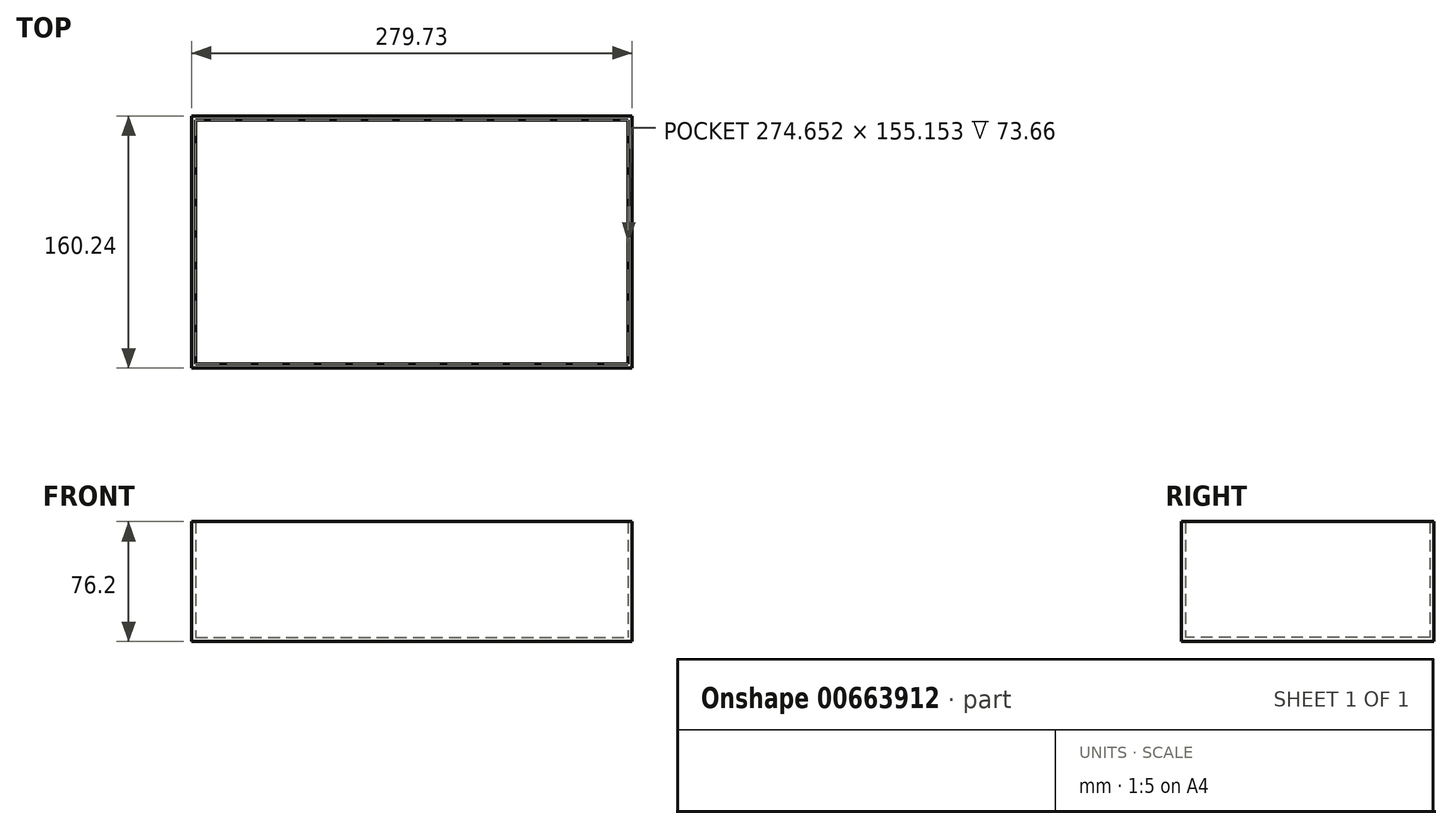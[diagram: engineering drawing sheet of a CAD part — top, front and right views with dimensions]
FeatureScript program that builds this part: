
annotation { "Feature Type Name" : "Feature", "Feature Type Description" : "" }
export const myFeature = defineFeature(function(context is Context, id is Id, definition is map)
    precondition{}
    {
        {
            var Q0;
            Q0=qCreatedBy(makeId("Right.planeOp"),FACE);
            var sketch = newSketch(context, id + "F0", { "sketchPlane" : qUnion([Q0])});
            skLineSegment(sketch, "E0.bottom", {"start": v(-105.78, 33) * mm, "end": v(26.82, 33) * mm});
            skLineSegment(sketch, "E0.top", {"start": v(-105.78, -57.7) * mm, "end": v(26.82, -57.7) * mm});
            skLineSegment(sketch, "E0.left", {"start": v(-105.78, 33) * mm, "end": v(-105.78, -57.7) * mm});
            skLineSegment(sketch, "E0.right", {"start": v(26.82, 33) * mm, "end": v(26.82, -57.7) * mm});
            skSolve(sketch);
        }
        {
            var Q0;
            Q0 = qSketchRegion(id + "F0", true);
            extrude(context, id + "F1", {"entities" : qUnion([Q0]), "depth" : 76.2 * mm, "offsetDistance" : 25.4 * mm});
        }
        {
            var Q0;
            Q0=makeQuery(id+"F1.opExtrude","SWEPT_BODY",BODY,{"disambiguationData":[OSD([sQuery(id+"F0.wireOp",EDGE,"E0.bottom"),sQuery(id+"F0.wireOp",EDGE,"E0.top"),sQuery(id+"F0.wireOp",EDGE,"E0.left"),sQuery(id+"F0.wireOp",EDGE,"E0.right")])]});
            deleteBodies(context, id + "F2", {"entities" : qUnion([Q0])});
        }
        {
            var Q0;
            Q0=qCreatedBy(makeId("Top.planeOp"),FACE);
            var sketch = newSketch(context, id + "F3", { "sketchPlane" : qUnion([Q0])});
            skLineSegment(sketch, "E1.bottom", {"start": v(-160.94, 108.93) * mm, "end": v(118.8, 108.93) * mm});
            skLineSegment(sketch, "E1.top", {"start": v(-160.94, -51.3) * mm, "end": v(118.8, -51.3) * mm});
            skLineSegment(sketch, "E1.left", {"start": v(-160.94, 108.93) * mm, "end": v(-160.94, -51.3) * mm});
            skLineSegment(sketch, "E1.right", {"start": v(118.8, 108.93) * mm, "end": v(118.8, -51.3) * mm});
            skSolve(sketch);
        }
        {
            var Q0;
            Q0=makeQuery(id+"F3.imprint","IMPRINT",FACE,{"disambiguationData":[TD([[makeQuery(id+"F3.imprint","IMPRINT",EDGE,{"derivedFrom":sQuery(id+"F3.wireOp",EDGE,"E1.bottom")}),-1.0]])]});
            extrude(context, id + "F4", {"entities" : qUnion([Q0]), "depth" : 76.2 * mm, "offsetDistance" : 25.4 * mm});
        }
        {
            var Q0;
            Q0=makeQuery(id+"F4.opExtrude","CAP_FACE",FACE,{"disambiguationData":[OSD([sQuery(id+"F3.wireOp",EDGE,"E1.bottom"),sQuery(id+"F3.wireOp",EDGE,"E1.top"),sQuery(id+"F3.wireOp",EDGE,"E1.left"),sQuery(id+"F3.wireOp",EDGE,"E1.right")])],"isStart":false});
            shell(context, id + "F5", {"entities" : qUnion([Q0]), "thickness" : 2.54 * mm});
        }
    });
